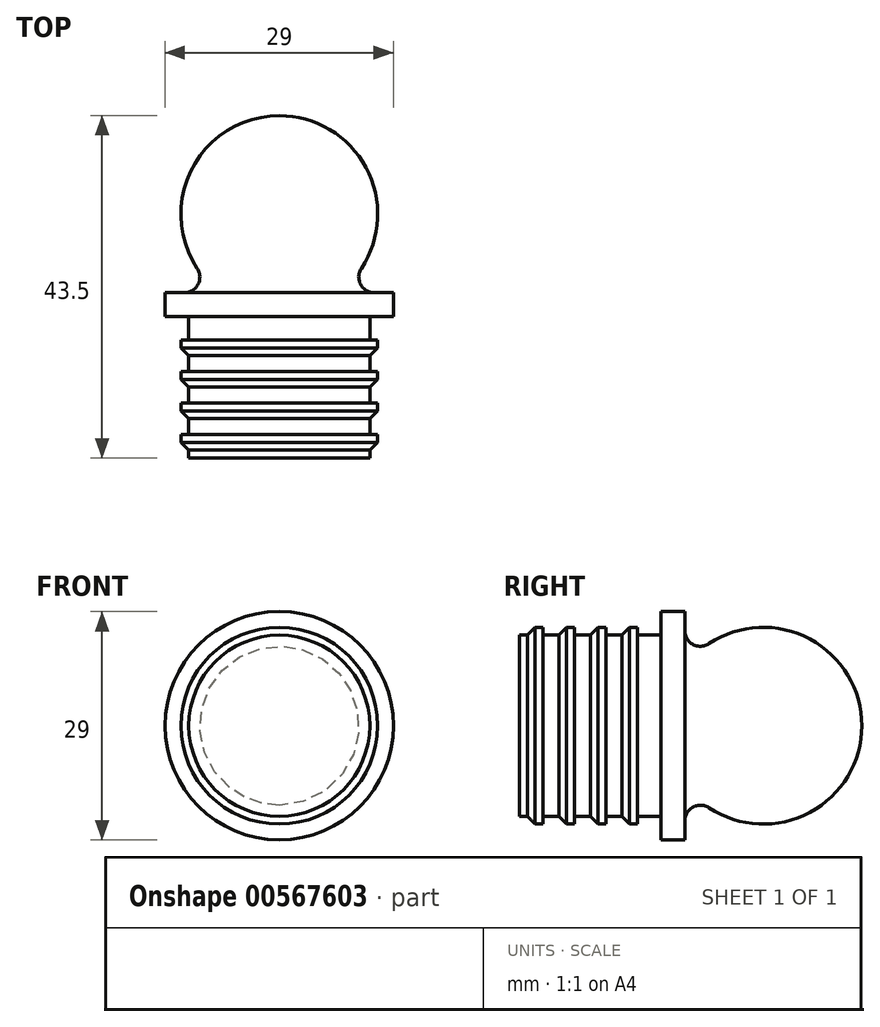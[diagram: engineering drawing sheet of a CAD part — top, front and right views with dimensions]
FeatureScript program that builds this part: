
annotation { "Feature Type Name" : "Feature", "Feature Type Description" : "" }
export const myFeature = defineFeature(function(context is Context, id is Id, definition is map)
    precondition{}
    {
        {
            var Q0;
            Q0=qCreatedBy(makeId("Top.planeOp"),FACE);
            var sketch = newSketch(context, id + "F0", { "sketchPlane" : qUnion([Q0])});
            skLineSegment(sketch, "E0", {"start": v(0, 0) * mm, "end": v(0, 21) * mm});
            skLineSegment(sketch, "E1", {"start": v(0, 21) * mm, "end": v(14.5, 21) * mm});
            skLineSegment(sketch, "E2", {"start": v(14.5, 21) * mm, "end": v(14.5, 18) * mm});
            skLineSegment(sketch, "E3", {"start": v(14.5, 18) * mm, "end": v(11.5, 18) * mm});
            skLineSegment(sketch, "E4", {"start": v(0, 0) * mm, "end": v(11.5, 0) * mm});
            skLineSegment(sketch, "E5", {"start": v(11.5, 0) * mm, "end": v(11.5, 18) * mm});
            skLineSegment(sketch, "E6.bottom", {"start": v(11.5, 15) * mm, "end": v(12.5, 15) * mm});
            skLineSegment(sketch, "E6.top", {"start": v(11.5, 14) * mm, "end": v(12.5, 14) * mm});
            skLineSegment(sketch, "E6.left", {"start": v(11.5, 15) * mm, "end": v(11.5, 14) * mm});
            skLineSegment(sketch, "E6.right", {"start": v(12.5, 15) * mm, "end": v(12.5, 14) * mm});
            skLineSegment(sketch, "E7.0.1.0", {"start": v(12.5, 11) * mm, "end": v(12.5, 10) * mm});
            skLineSegment(sketch, "E7.0.1.1", {"start": v(11.5, 10) * mm, "end": v(12.5, 10) * mm});
            skLineSegment(sketch, "E7.0.1.2", {"start": v(11.5, 11) * mm, "end": v(12.5, 11) * mm});
            skLineSegment(sketch, "E7.0.1.3", {"start": v(11.5, 11) * mm, "end": v(11.5, 10) * mm});
            skLineSegment(sketch, "E7.0.2.0", {"start": v(12.5, 7) * mm, "end": v(12.5, 6) * mm});
            skLineSegment(sketch, "E7.0.2.1", {"start": v(11.5, 6) * mm, "end": v(12.5, 6) * mm});
            skLineSegment(sketch, "E7.0.2.2", {"start": v(11.5, 7) * mm, "end": v(12.5, 7) * mm});
            skLineSegment(sketch, "E7.0.2.3", {"start": v(11.5, 7) * mm, "end": v(11.5, 6) * mm});
            skLineSegment(sketch, "E7.0.3.0", {"start": v(12.5, 3) * mm, "end": v(12.5, 2) * mm});
            skLineSegment(sketch, "E7.0.3.1", {"start": v(11.5, 2) * mm, "end": v(12.5, 2) * mm});
            skLineSegment(sketch, "E7.0.3.2", {"start": v(11.5, 3) * mm, "end": v(12.5, 3) * mm});
            skLineSegment(sketch, "E7.0.3.3", {"start": v(11.5, 3) * mm, "end": v(11.5, 2) * mm});
            skLineSegment(sketch, "E7.direction1", {"start": v(11.5, 14) * mm, "end": v(14.6, 14) * mm, "construction": true});
            skLineSegment(sketch, "E7.direction2", {"start": v(11.5, 14) * mm, "end": v(11.5, 10) * mm, "construction": true});
            skSolve(sketch);
        }
        {
            var Q0;
            Q0=makeQuery(id+"F0.imprint","IMPRINT",FACE,{"disambiguationData":[TD([[makeQuery(id+"F0.imprint","IMPRINT",EDGE,{"derivedFrom":sQuery(id+"F0.wireOp",EDGE,"E0")}),-1.0]])]});
            var Q1;
            Q1=makeQuery(id+"F0.imprint","IMPRINT",FACE,{"disambiguationData":[TD([[makeQuery(id+"F0.imprint","IMPRINT",EDGE,{"derivedFrom":sQuery(id+"F0.wireOp",EDGE,"E6.bottom")}),-1.0]])]});
            var Q2;
            Q2=makeQuery(id+"F0.imprint","IMPRINT",FACE,{"disambiguationData":[TD([[makeQuery(id+"F0.imprint","IMPRINT",EDGE,{"derivedFrom":sQuery(id+"F0.wireOp",EDGE,"E7.0.1.0")}),-1.0]])]});
            var Q3;
            Q3=makeQuery(id+"F0.imprint","IMPRINT",FACE,{"disambiguationData":[TD([[makeQuery(id+"F0.imprint","IMPRINT",EDGE,{"derivedFrom":sQuery(id+"F0.wireOp",EDGE,"E7.0.2.0")}),-1.0]])]});
            var Q4;
            Q4=makeQuery(id+"F0.imprint","IMPRINT",FACE,{"disambiguationData":[TD([[makeQuery(id+"F0.imprint","IMPRINT",EDGE,{"derivedFrom":sQuery(id+"F0.wireOp",EDGE,"E7.0.3.0")}),-1.0]])]});
            var Q5;
            Q5=sQuery(id+"F0.wireOp",EDGE,"E0");
            revolve(context, id + "F1", {"entities" : qUnion([Q0, Q1, Q2, Q3, Q4]), "axis" : qUnion([Q5]), "revolveType" : RevolveType.FULL});
        }
        {
            var Q0;
            Q0=makeQuery(id+"F1.opRevolve","SWEPT_EDGE",EDGE,{"disambiguationData":[OSD([sQuery(id+"F0.wireOp",EDGE,"E5"),sQuery(id+"F0.wireOp",EDGE,"E7.0.3.1"),sQuery(id+"F0.wireOp",EDGE,"E7.0.3.3")])]});
            var Q1;
            Q1=makeQuery(id+"F1.opRevolve","SWEPT_EDGE",EDGE,{"disambiguationData":[OSD([sQuery(id+"F0.wireOp",EDGE,"E5"),sQuery(id+"F0.wireOp",EDGE,"E7.0.2.1"),sQuery(id+"F0.wireOp",EDGE,"E7.0.2.3")])]});
            var Q2;
            Q2=makeQuery(id+"F1.opRevolve","SWEPT_EDGE",EDGE,{"disambiguationData":[OSD([sQuery(id+"F0.wireOp",EDGE,"E5"),sQuery(id+"F0.wireOp",EDGE,"E7.0.1.1"),sQuery(id+"F0.wireOp",EDGE,"E7.0.1.3")])]});
            var Q3;
            Q3=makeQuery(id+"F1.opRevolve","SWEPT_EDGE",EDGE,{"disambiguationData":[OSD([sQuery(id+"F0.wireOp",EDGE,"E5"),sQuery(id+"F0.wireOp",EDGE,"E6.top"),sQuery(id+"F0.wireOp",EDGE,"E6.left")])]});
            chamfer(context, id + "F2", {"entities" : qUnion([Q0, Q1, Q2, Q3]), "width" : 1 * mm, "tangentPropagation" : true});
        }
        {
            var Q0;
            Q0=qCreatedBy(makeId("Top.planeOp"),FACE);
            var sketch = newSketch(context, id + "F3", { "sketchPlane" : qUnion([Q0])});
            skCircle(sketch, "E8", {"center": v(0, 31) * mm, "radius": 12.5 * mm});
            skLineSegment(sketch, "E9", {"start": v(0, 43.5) * mm, "end": v(0, 18.5) * mm});
            skSolve(sketch);
        }
        {
            var Q0;
            {var subQ0=sQuery(id+"F3.wireOp",EDGE,"E9");Q0=makeQuery(id+"F3.imprint","IMPRINT",FACE,{"disambiguationData":[TD([[makeQuery(id+"F3.imprint","IMPRINT",EDGE,{"derivedFrom":subQ0}),1.0]])]});}
            var Q1;
            Q1=sQuery(id+"F3.wireOp",EDGE,"E9");
            revolve(context, id + "F4", {"operationType" : NewBodyOperationType.ADD, "entities" : qUnion([Q0]), "axis" : qUnion([Q1]), "revolveType" : RevolveType.FULL});
        }
        {
            var Q0;
            Q0=makeQuery(id+"F4.boolean.opBoolean","INTERSECT",EDGE,{"derivedFrom":[makeQuery(id+"F1.opRevolve","SWEPT_FACE",FACE,{"disambiguationData":[OSD([sQuery(id+"F0.wireOp",EDGE,"E1")])]}),makeQuery(id+"F4.opRevolve","SWEPT_FACE",FACE,{"disambiguationData":[OSD([sQuery(id+"F3.wireOp",EDGE,"E8")])]})]});
            fillet(context, id + "F5", {"entities" : qUnion([Q0]), "radius" : 2 * mm, "tangentPropagation" : true, "allowEdgeOverflow" : false});
        }
    });
